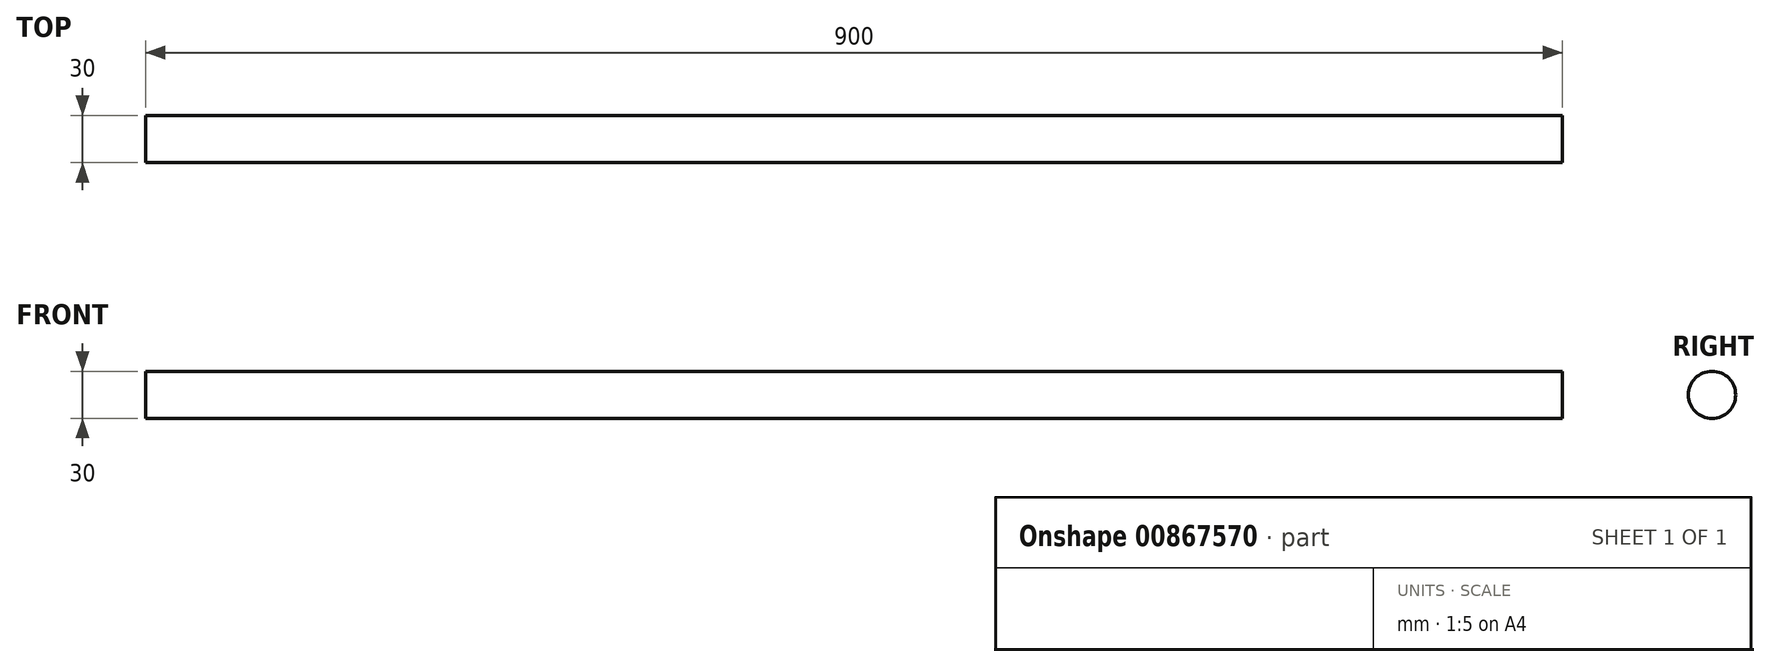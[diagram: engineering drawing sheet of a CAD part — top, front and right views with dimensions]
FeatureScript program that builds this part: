
annotation { "Feature Type Name" : "Feature", "Feature Type Description" : "" }
export const myFeature = defineFeature(function(context is Context, id is Id, definition is map)
    precondition{}
    {
        {
            var Q0;
            Q0=qCreatedBy(makeId("Right.planeOp"),FACE);
            var sketch = newSketch(context, id + "F0", { "sketchPlane" : qUnion([Q0])});
            skCircle(sketch, "E0", {"center": v(0, 0) * mm, "radius": 15 * mm});
            skSolve(sketch);
        }
        {
            var Q0;
            Q0=makeQuery(id+"F0.imprint","IMPRINT",FACE,{"disambiguationData":[TD([[makeQuery(id+"F0.imprint","IMPRINT",EDGE,{"derivedFrom":sQuery(id+"F0.wireOp",EDGE,"E0")}),1.0]])]});
            extrude(context, id + "F1", {"entities" : qUnion([Q0]), "endBound" : BoundingType.SYMMETRIC, "depth" : 900 * mm, "offsetDistance" : 25 * mm});
        }
    });
